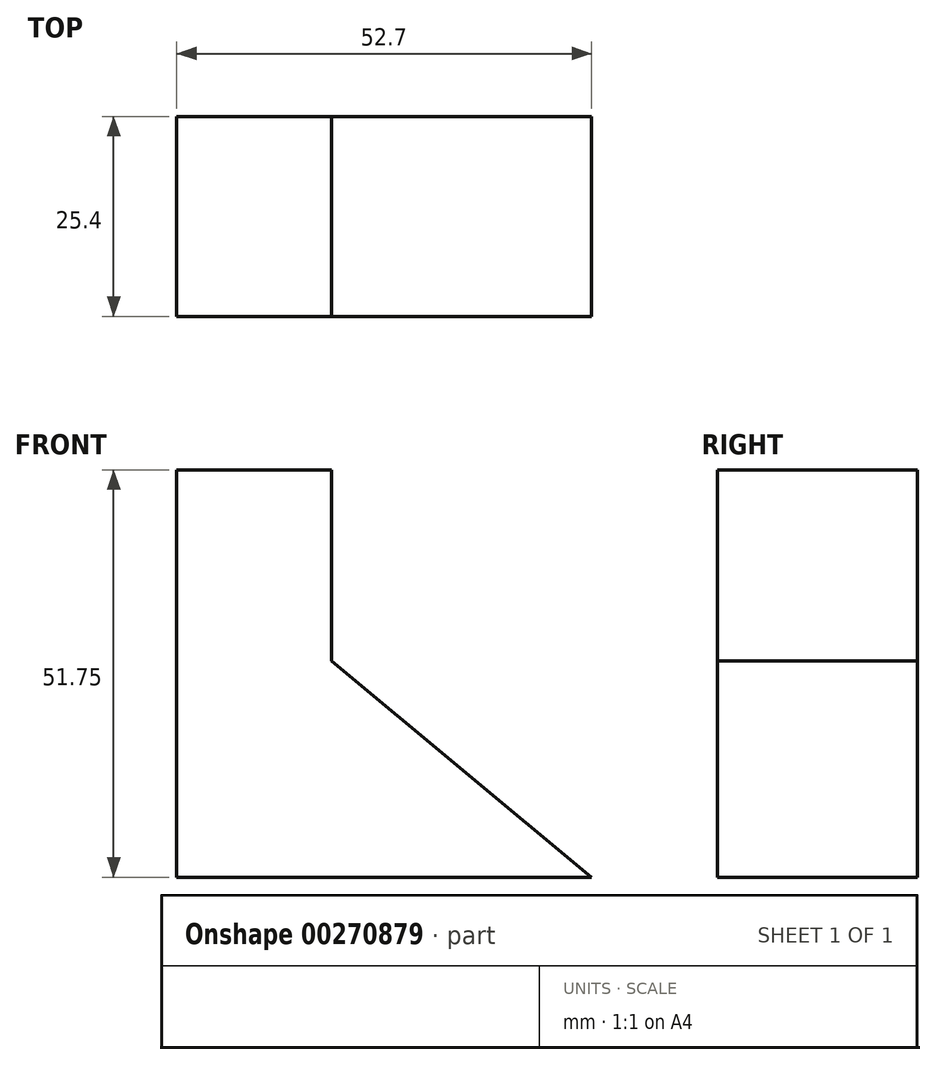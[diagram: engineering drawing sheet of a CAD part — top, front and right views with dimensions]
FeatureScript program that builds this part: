
annotation { "Feature Type Name" : "Feature", "Feature Type Description" : "" }
export const myFeature = defineFeature(function(context is Context, id is Id, definition is map)
    precondition{}
    {
        {
            var Q0;
            Q0=qCreatedBy(makeId("Front.planeOp"),FACE);
            var sketch = newSketch(context, id + "F0", { "sketchPlane" : qUnion([Q0])});
            skLineSegment(sketch, "E0.bottom", {"start": v(0, 0) * mm, "end": v(-52.7, 0) * mm});
            skLineSegment(sketch, "E0.top", {"start": v(0, 0) * mm, "end": v(-52.7, 0) * mm});
            skLineSegment(sketch, "E0.left", {"start": v(0, 0) * mm, "end": v(0, 0) * mm});
            skLineSegment(sketch, "E0.right", {"start": v(-52.7, 0) * mm, "end": v(-52.7, 0) * mm});
            skLineSegment(sketch, "E1.bottom", {"start": v(-52.7, 51.75) * mm, "end": v(-52.7, 51.75) * mm});
            skLineSegment(sketch, "E1.left", {"start": v(-52.7, 51.75) * mm, "end": v(-52.7, 0) * mm});
            skLineSegment(sketch, "E1.right", {"start": v(-52.7, 51.75) * mm, "end": v(-52.7, 0) * mm});
            skLineSegment(sketch, "E2.bottom", {"start": v(-52.7, 51.75) * mm, "end": v(-33.04, 51.75) * mm});
            skLineSegment(sketch, "E2.top", {"start": v(-52.7, 51.75) * mm, "end": v(-33.04, 51.75) * mm});
            skLineSegment(sketch, "E2.right", {"start": v(-33.04, 51.75) * mm, "end": v(-33.04, 51.75) * mm});
            skLineSegment(sketch, "E3.bottom", {"start": v(-33.04, 27.5) * mm, "end": v(-33.04, 27.5) * mm});
            skLineSegment(sketch, "E3.left", {"start": v(-33.04, 27.5) * mm, "end": v(-33.04, 51.75) * mm});
            skLineSegment(sketch, "E3.right", {"start": v(-33.04, 27.5) * mm, "end": v(-33.04, 51.75) * mm});
            skLineSegment(sketch, "E4", {"start": v(-33.04, 27.5) * mm, "end": v(0, 0) * mm});
            skSolve(sketch);
        }
        {
            var Q0;
            Q0 = qSketchRegion(id + "F0", true);
            extrude(context, id + "F1", {"entities" : qUnion([Q0]), "depth" : 25.4 * mm});
        }
    });
